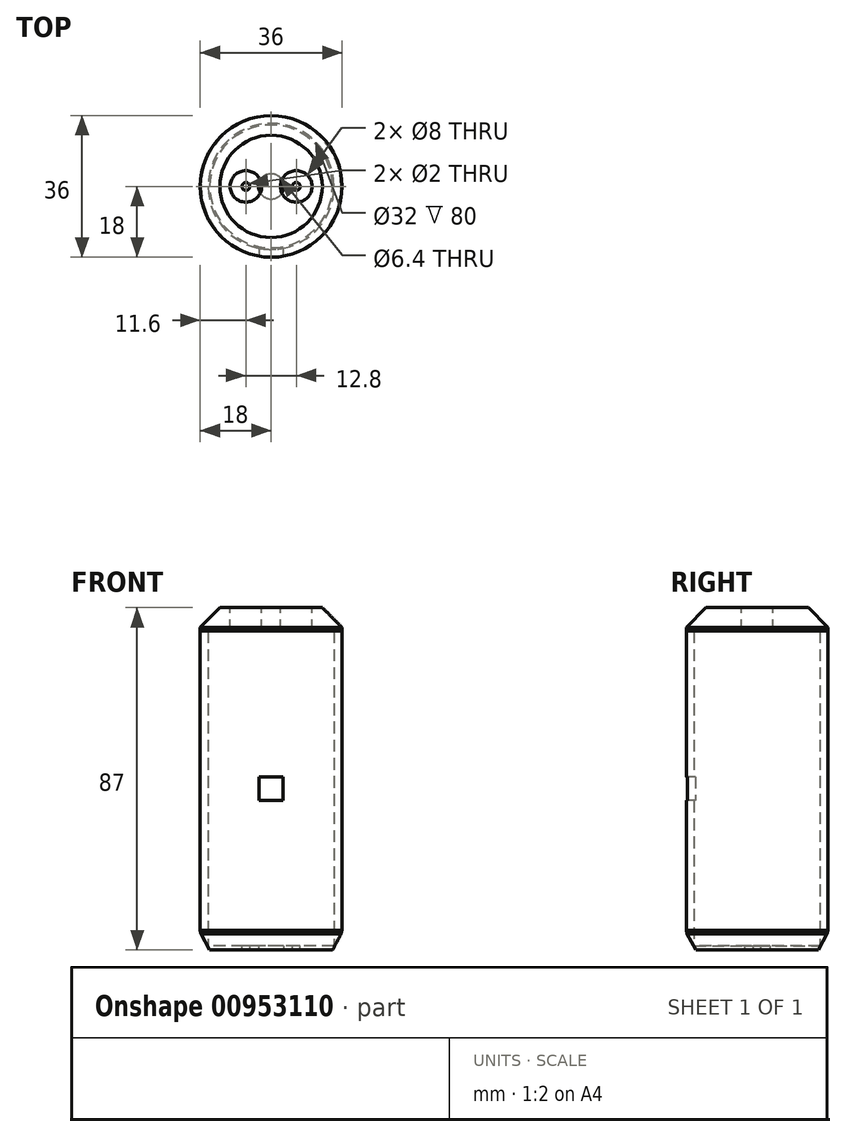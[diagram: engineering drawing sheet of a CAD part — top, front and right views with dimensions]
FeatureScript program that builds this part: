
annotation { "Feature Type Name" : "Feature", "Feature Type Description" : "" }
export const myFeature = defineFeature(function(context is Context, id is Id, definition is map)
    precondition{}
    {
        {
            var Q0;
            Q0=qCreatedBy(makeId("Top.planeOp"),FACE);
            var sketch = newSketch(context, id + "F0", { "sketchPlane" : qUnion([Q0])});
            skCircle(sketch, "E0", {"center": v(0, 0) * mm, "radius": 3.2 * mm});
            skCircle(sketch, "E1", {"center": v(0, 0) * mm, "radius": 18 * mm});
            skSolve(sketch);
        }
        {
            var Q0;
            Q0=makeQuery(id+"F0.imprint","IMPRINT",FACE,{"disambiguationData":[TD([[makeQuery(id+"F0.imprint","IMPRINT",EDGE,{"derivedFrom":sQuery(id+"F0.wireOp",EDGE,"E0")}),-1.0]])]});
            extrude(context, id + "F1", {"entities" : qUnion([Q0]), "depth" : 1 * mm, "offsetDistance" : 25 * mm});
        }
        {
            var Q0;
            Q0=qCreatedBy(makeId("Front.planeOp"),FACE);
            cPlane(context, id + "F2", {"entities" : qUnion([Q0]), "cplaneType" : CPlaneType.OFFSET, "offset" : 18 * mm, "width" : 150 * mm, "height" : 150 * mm});
        }
        {
            var Q0;
            Q0=makeQuery(id+"F1.opExtrude","CAP_FACE",FACE,{"disambiguationData":[OSD([sQuery(id+"F0.wireOp",EDGE,"E0"),sQuery(id+"F0.wireOp",EDGE,"E1")])],"isStart":false});
            var sketch = newSketch(context, id + "F3", { "sketchPlane" : qUnion([Q0])});
            skCircle(sketch, "E2", {"center": v(0, 0) * mm, "radius": 16 * mm});
            skCircle(sketch, "E3", {"center": v(-6.4, 0) * mm, "radius": 1 * mm});
            skCircle(sketch, "E4", {"center": v(6.4, 0) * mm, "radius": 1 * mm});
            skSolve(sketch);
        }
        {
            var Q0;
            Q0=makeQuery(id+"F3.imprint","IMPRINT",FACE,{"disambiguationData":[TD([[makeQuery(id+"F3.imprint","IMPRINT",EDGE,{"derivedFrom":sQuery(id+"F3.wireOp",EDGE,"E3")}),1.0]])]});
            var Q1;
            Q1=makeQuery(id+"F3.imprint","IMPRINT",FACE,{"disambiguationData":[TD([[makeQuery(id+"F3.imprint","IMPRINT",EDGE,{"derivedFrom":sQuery(id+"F3.wireOp",EDGE,"E4")}),1.0]])]});
            extrude(context, id + "F4", {"entities" : qUnion([Q0, Q1]), "operationType" : NewBodyOperationType.REMOVE, "oppositeDirection" : true, "depth" : 25 * mm, "offsetDistance" : 25 * mm});
        }
        {
            var Q0;
            Q0=makeQuery(id+"F3.imprint","IMPRINT",FACE,{"disambiguationData":[TD([[makeQuery(id+"F3.imprint","IMPRINT",EDGE,{"derivedFrom":sQuery(id+"F3.wireOp",EDGE,"E2")}),-1.0]])]});
            extrude(context, id + "F5", {"entities" : qUnion([Q0]), "operationType" : NewBodyOperationType.ADD, "depth" : 80 * mm, "offsetDistance" : 25 * mm});
        }
        {
            var Q0;
            Q0=qCreatedBy(id+"F2.planeOp",FACE);
            var sketch = newSketch(context, id + "F6", { "sketchPlane" : qUnion([Q0])});
            skLineSegment(sketch, "E5.bottom", {"start": v(-3, 44) * mm, "end": v(3, 44) * mm});
            skLineSegment(sketch, "E5.top", {"start": v(-3, 38) * mm, "end": v(3, 38) * mm});
            skLineSegment(sketch, "E5.left", {"start": v(-3, 44) * mm, "end": v(-3, 38) * mm});
            skLineSegment(sketch, "E5.right", {"start": v(3, 44) * mm, "end": v(3, 38) * mm});
            skLineSegment(sketch, "E6", {"start": v(0, 44) * mm, "end": v(0, 38) * mm, "construction": true});
            skSolve(sketch);
        }
        {
            var Q0;
            Q0=makeQuery(id+"F6.imprint","IMPRINT",FACE,{"disambiguationData":[TD([[makeQuery(id+"F6.imprint","IMPRINT",EDGE,{"derivedFrom":sQuery(id+"F6.wireOp",EDGE,"E5.bottom")}),-1.0]])]});
            extrude(context, id + "F7", {"entities" : qUnion([Q0]), "operationType" : NewBodyOperationType.REMOVE, "oppositeDirection" : true, "depth" : 25 * mm, "offsetDistance" : 25 * mm});
        }
        {
            var Q0;
            Q0=makeQuery(id+"F5.opExtrude","CAP_FACE",FACE,{"disambiguationData":[OSD([sQuery(id+"F0.wireOp",EDGE,"E1"),sQuery(id+"F3.wireOp",EDGE,"E2")])],"isStart":false});
            var sketch = newSketch(context, id + "F8", { "sketchPlane" : qUnion([Q0])});
            skCircle(sketch, "E7", {"center": v(0, 0) * mm, "radius": 18 * mm});
            skSolve(sketch);
        }
        {
            var Q0;
            Q0=makeQuery(id+"F8.imprint","IMPRINT",FACE,{"disambiguationData":[TD([[makeQuery(id+"F8.imprint","IMPRINT",EDGE,{"derivedFrom":sQuery(id+"F8.wireOp",EDGE,"E7")}),1.0]])]});
            var Q1;
            Q1=makeQuery(id+"F8.imprint","IMPRINT",FACE,{"disambiguationData":[TD([[makeQuery(id+"F8.imprint","IMPRINT",EDGE,{"derivedFrom":makeQuery(id+"F5.opExtrude","CAP_EDGE",EDGE,{"disambiguationData":[OSD([sQuery(id+"F3.wireOp",EDGE,"E2")])],"isStart":false})}),1.0]])]});
            extrude(context, id + "F9", {"entities" : qUnion([Q0, Q1]), "depth" : 6 * mm, "offsetDistance" : 25 * mm});
        }
        {
            var Q0;
            Q0=makeQuery(id+"F9.opExtrude","CAP_FACE",FACE,{"disambiguationData":[OSD([sQuery(id+"F8.wireOp",EDGE,"E7")])],"isStart":false});
            var sketch = newSketch(context, id + "F10", { "sketchPlane" : qUnion([Q0])});
            skCircle(sketch, "E8", {"center": v(-6.4, 0) * mm, "radius": 4 * mm});
            skCircle(sketch, "E9", {"center": v(6.4, 0) * mm, "radius": 4 * mm});
            skSolve(sketch);
        }
        {
            var Q0;
            Q0=makeQuery(id+"F10.imprint","IMPRINT",FACE,{"disambiguationData":[TD([[makeQuery(id+"F10.imprint","IMPRINT",EDGE,{"derivedFrom":sQuery(id+"F10.wireOp",EDGE,"E8")}),1.0]])]});
            var Q1;
            Q1=makeQuery(id+"F10.imprint","IMPRINT",FACE,{"disambiguationData":[TD([[makeQuery(id+"F10.imprint","IMPRINT",EDGE,{"derivedFrom":sQuery(id+"F10.wireOp",EDGE,"E9")}),1.0]])]});
            extrude(context, id + "F11", {"entities" : qUnion([Q0, Q1]), "operationType" : NewBodyOperationType.REMOVE, "oppositeDirection" : true, "depth" : 25 * mm, "offsetDistance" : 25 * mm});
        }
        {
            var Q0;
            Q0=makeQuery(id+"F9.opExtrude","CAP_EDGE",EDGE,{"disambiguationData":[OSD([sQuery(id+"F8.wireOp",EDGE,"E7")])],"isStart":false});
            chamfer(context, id + "F12", {"entities" : qUnion([Q0]), "width" : 5 * mm, "tangentPropagation" : true});
        }
        {
            var Q0;
            Q0=makeQuery(id+"F1.opExtrude","CAP_EDGE",EDGE,{"disambiguationData":[OSD([sQuery(id+"F0.wireOp",EDGE,"E1")])],"isStart":true});
            chamfer(context, id + "F13", {"entities" : qUnion([Q0]), "chamferType" : ChamferType.OFFSET_ANGLE, "width" : 4.5 * mm, "oppositeDirection" : false, "angle" : 28 * degree, "tangentPropagation" : true});
        }
        {
            var Q0;
            {var subQ0=sQuery(id+"F0.wireOp",EDGE,"E1");Q0=makeQuery(id+"F13.opChamfer","BLEND_EDGE",EDGE,{"blendedFrom":[makeQuery(id+"F1.opExtrude","CAP_EDGE",EDGE,{"disambiguationData":[OSD([subQ0])],"isStart":true}),makeQuery(id+"F5.boolean.opBoolean","MERGE",FACE,{"derivedFrom":[makeQuery(id+"F1.opExtrude","SWEPT_FACE",FACE,{"disambiguationData":[OSD([subQ0])]}),makeQuery(id+"F5.opExtrude","SWEPT_FACE",FACE,{"disambiguationData":[OSD([subQ0])]})]})],"blendedInto":[makeQuery(id+"F5.boolean.opBoolean","MERGE",FACE,{"derivedFrom":[makeQuery(id+"F1.opExtrude","SWEPT_FACE",FACE,{"disambiguationData":[OSD([subQ0])]}),makeQuery(id+"F5.opExtrude","SWEPT_FACE",FACE,{"disambiguationData":[OSD([subQ0])]})]})]});}
            chamfer(context, id + "F14", {"entities" : qUnion([Q0]), "width" : 2 * mm, "tangentPropagation" : true});
        }
    });
